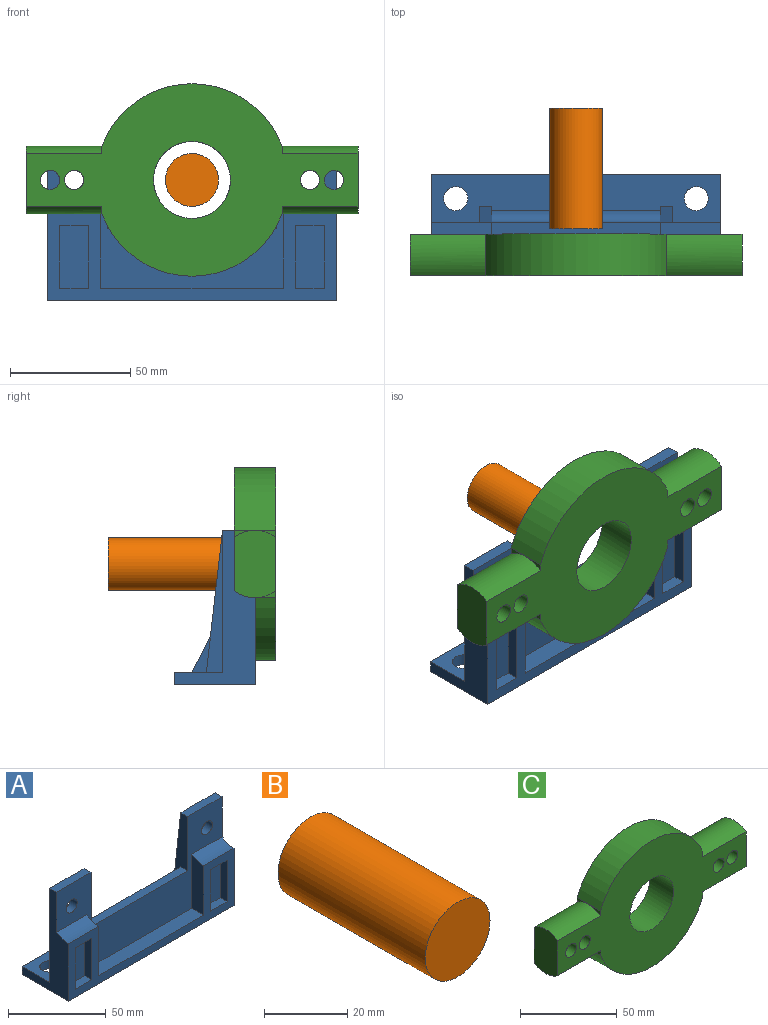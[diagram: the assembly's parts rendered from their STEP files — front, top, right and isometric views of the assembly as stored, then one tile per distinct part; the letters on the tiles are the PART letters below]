
ASSEMBLY  parts=3 mates=2
PART A: 63 faces, bbox 120x33.6x64 mm
  f0: plane 59x20mm, normal (0,1,0), area 1129.7mm2, adj f1,f11,f13,f19,f31
  f1: plane 120x20mm, normal (0,0,1), area 1786.8mm2, adj f0,f5,f9,f10,f11,f16,f17,f22
  f2: plane 32.5x20mm, normal (0,1,0), area 425mm2, adj f3,f9,f25,f33,f58,f59,f60,f61
  f3: plane 70x5mm, normal (0,0,1), area 350mm2, adj f2,f4,f7,f9,f24,f27
  f4: plane 32.5x20mm, normal (0,1,0), area 425mm2, adj f3,f26,f27,f32,f53,f54,f55,f56
  f5: plane 59x20mm, normal (0,1,0), area 1129.7mm2, adj f1,f8,f18,f22,f29
  f6: plane 76x8.6mm, normal (0,0,1), area 653.6mm2, adj f7,f12,f14,f23
  f7: plane 120x59mm, normal (0,-1,0), area 3105.5mm2, adj f3,f6,f8,f9,f11,f12,f13,f18
  f8: plane 25x5mm, normal (0,0,1), area 125mm2, adj f5,f7,f9,f22,f28
  f9: plane 59x11.73mm, normal (-1,0,0), area 363.3mm2, adj f1,f2,f3,f7,f8,f28,f33
  f10: plane 120x5mm, normal (0,1,0), area 600mm2, adj f1,f11,f15,f22
  f11: plane 64x33.6mm, normal (-1,0,0), area 737.7mm2, adj f0,f1,f7,f10,f13,f14,f15,f20
  f12: plane 33.95x8.6mm, normal (1,0,0), area 274.7mm2, adj f6,f7,f14,f20
  f13: plane 25x5mm, normal (0,0,1), area 125mm2, adj f0,f7,f11,f27,f30
  f14: plane 120x36mm, normal (0,-1,0), area 1340mm2, adj f6,f11,f12,f15,f20,f21,f22,f23
  f15: plane 120x33.6mm, normal (0,0,-1), area 1790.9mm2, adj f10,f11,f14,f16,f17,f22,f34,f35
  f16: cylinder r=5mm len=10mm, axis (0,0,1), area 157.1mm2, adj f1,f15
  f17: cylinder r=5mm len=10mm, axis (0,0,1), area 157.1mm2, adj f1,f15
  f18: cylinder r=4mm len=8mm, axis (0,1,0), area 125.7mm2, adj f5,f7
  f19: cylinder r=4mm len=8mm, axis (0,1,0), area 125.7mm2, adj f0,f7
  f20: cylinder r=14mm len=22mm, axis (1,0,0), area 203.7mm2, adj f7,f11,f12,f14
  f21: cylinder r=14mm len=22mm, axis (-1,0,0), area 203.7mm2, adj f7,f14,f22,f23
  f22: plane 64x33.6mm, normal (1,0,0), area 737.7mm2, adj f1,f5,f7,f8,f10,f14,f15,f21
  f23: plane 33.95x8.6mm, normal (-1,0,0), area 274.7mm2, adj f6,f7,f14,f21
  f24: plane 25x12.75mm, normal (0,0.89,0.45), area 140.3mm2, adj f1,f3,f25,f26
  f25: plane 25x12.75mm, normal (1,0,0), area 154mm2, adj f1,f2,f24,f33
  f26: plane 25x12.75mm, normal (-1,0,0), area 154mm2, adj f1,f4,f24,f32
  f27: plane 59x11.73mm, normal (1,0,0), area 363.3mm2, adj f1,f3,f4,f7,f13,f30,f32
  f28: plane 59x6.73mm, normal (0,0.99,0.11), area 296.9mm2, adj f1,f8,f9,f29
  f29: plane 59x6.73mm, normal (1,0,0), area 198.7mm2, adj f1,f5,f28
  f30: plane 59x6.73mm, normal (0,0.99,0.11), area 296.9mm2, adj f1,f13,f27,f31
  f31: plane 59x6.73mm, normal (-1,0,0), area 198.7mm2, adj f0,f1,f30
  f32: cylinder r=5mm len=32.5mm, axis (1,0,0), area 255.3mm2, adj f1,f4,f26,f27
  f33: cylinder r=5mm len=32.5mm, axis (1,0,0), area 255.3mm2, adj f1,f2,f9,f25
  f34: plane 16x2mm, normal (0,-1,0), area 32mm2, adj f15,f35,f41,f42
  f35: plane 16x2mm, normal (1,0,0), area 32mm2, adj f15,f34,f36,f42
  f36: plane 78x2mm, normal (0,-1,0), area 156mm2, adj f15,f35,f37,f42
  f37: plane 16x2mm, normal (-1,0,0), area 32mm2, adj f15,f36,f38,f42
  f38: plane 16x2mm, normal (0,-1,0), area 32mm2, adj f15,f37,f39,f42
  f39: plane 7.6x2mm, normal (-1,0,0), area 15.2mm2, adj f15,f38,f40,f42
  f40: plane 110x2mm, normal (0,1,0), area 220mm2, adj f15,f39,f41,f42
  f41: plane 7.6x2mm, normal (1,0,0), area 15.2mm2, adj f15,f34,f40,f42
  f42: plane 110x23.6mm, normal (0,0,-1), area 2084mm2, adj f34,f35,f36,f37,f38,f39,f40,f41
  f43: plane 26x5mm, normal (1,0,0), area 130mm2, adj f14,f44,f46,f47
  f44: plane 12x5mm, normal (0,0,1), area 60mm2, adj f14,f43,f45,f47
  f45: plane 26x5mm, normal (-1,0,0), area 130mm2, adj f14,f44,f46,f47
  f46: plane 12x5mm, normal (0,0,-1), area 60mm2, adj f14,f43,f45,f47
  f47: plane 26x12mm, normal (0,-1,0), area 312mm2, adj f43,f44,f45,f46
  f48: plane 26x5mm, normal (1,0,0), area 130mm2, adj f14,f49,f51,f52
  f49: plane 12x5mm, normal (0,0,1), area 60mm2, adj f14,f48,f50,f52
  f50: plane 26x5mm, normal (-1,0,0), area 130mm2, adj f14,f49,f51,f52
  f51: plane 12x5mm, normal (0,0,-1), area 60mm2, adj f14,f48,f50,f52
  f52: plane 26x12mm, normal (0,-1,0), area 312mm2, adj f48,f49,f50,f51
  f53: plane 10x2mm, normal (-1,0,0), area 20mm2, adj f4,f54,f56,f57
  f54: plane 22.5x2mm, normal (0,0,1), area 45mm2, adj f4,f53,f55,f57
  f55: plane 10x2mm, normal (1,0,0), area 20mm2, adj f4,f54,f56,f57
  f56: plane 22.5x2mm, normal (0,0,-1), area 45mm2, adj f4,f53,f55,f57
  f57: plane 22.5x10mm, normal (0,1,0), area 225mm2, adj f53,f54,f55,f56
  f58: plane 10x2mm, normal (-1,0,0), area 20mm2, adj f2,f59,f61,f62
  f59: plane 22.5x2mm, normal (0,0,1), area 45mm2, adj f2,f58,f60,f62
  f60: plane 10x2mm, normal (1,0,0), area 20mm2, adj f2,f59,f61,f62
  f61: plane 22.5x2mm, normal (0,0,-1), area 45mm2, adj f2,f58,f60,f62
  f62: plane 22.5x10mm, normal (0,1,0), area 225mm2, adj f58,f59,f60,f61
PART B: 3 faces, bbox 22x50x22 mm
  f0: cylinder r=11mm len=50mm, axis (0,1,0), area 3455.8mm2, adj f1,f2
  f1: plane 22x22mm, normal (0,-1,0), area 380.1mm2, adj f0
  f2: plane 22x22mm, normal (0,1,0), area 380.1mm2, adj f0
PART C: 27 faces, bbox 138x17.2x80 mm
  f0: plane 138x80mm, normal (0,-1,0), area 5319.8mm2, adj f1,f2,f4,f5,f6,f7,f8,f9
  f1: plane 17.2x0.03mm, normal (0,0,1), area 0.5mm2, adj f0,f3,f12,f24,f26
  f2: plane 17.2x0.03mm, normal (0,0,-1), area 0.5mm2, adj f0,f3,f13,f22,f25
  f3: plane 138x80mm, normal (0,1,0), area 5319.8mm2, adj f1,f2,f4,f5,f6,f7,f8,f9
  f4: plane 28x17.2mm, normal (-1,0,0), area 449.3mm2, adj f0,f3,f15,f17
  f5: plane 17.2x0.03mm, normal (0,0,1), area 0.5mm2, adj f0,f3,f12,f18,f20
  f6: plane 17.2x0.03mm, normal (0,0,-1), area 0.5mm2, adj f0,f3,f13,f16,f19
  f7: plane 28x17.2mm, normal (1,0,0), area 449.3mm2, adj f0,f3,f21,f23
  f8: cylinder r=4mm len=17.2mm, axis (0,-1,0), area 432.3mm2, adj f0,f3
  f9: cylinder r=4mm len=17.2mm, axis (0,-1,0), area 432.3mm2, adj f0,f3
  f10: cylinder r=4mm len=17.2mm, axis (0,-1,0), area 432.3mm2, adj f0,f3
  f11: cylinder r=4mm len=17.2mm, axis (0,-1,0), area 432.3mm2, adj f0,f3
  f12: cylinder r=40mm len=74.94mm, axis (0,-1,0), area 1669.4mm2, adj f0,f1,f3,f5
  f13: cylinder r=40mm len=74.94mm, axis (0,-1,0), area 1669.4mm2, adj f0,f2,f3,f6
  f14: cylinder r=16mm len=32mm, axis (0,-1,0), area 1729.1mm2, adj f0,f3
  f15: cylinder r=14mm len=31.5mm, axis (-1,0,0), area 583.4mm2, adj f0,f3,f4,f16,f19
  f16: plane 8.6x2.95mm, normal (-1,0,0), area 8.1mm2, adj f0,f6,f15
  f17: cylinder r=14mm len=31.5mm, axis (-1,0,0), area 583.4mm2, adj f0,f3,f4,f18,f20
  f18: plane 8.6x2.95mm, normal (-1,0,0), area 8.1mm2, adj f0,f5,f17
  f19: plane 8.6x2.95mm, normal (-1,0,0), area 8.1mm2, adj f3,f6,f15
  f20: plane 8.6x2.95mm, normal (-1,0,0), area 8.1mm2, adj f3,f5,f17
  f21: cylinder r=14mm len=31.5mm, axis (1,0,0), area 583.4mm2, adj f0,f3,f7,f22,f25
  f22: plane 8.6x2.95mm, normal (1,0,0), area 8.1mm2, adj f2,f3,f21
  f23: cylinder r=14mm len=31.5mm, axis (1,0,0), area 583.4mm2, adj f0,f3,f7,f24,f26
  f24: plane 8.6x2.95mm, normal (1,0,0), area 8.1mm2, adj f1,f3,f23
  f25: plane 8.6x2.95mm, normal (1,0,0), area 8.1mm2, adj f0,f2,f21
  f26: plane 8.6x2.95mm, normal (1,0,0), area 8.1mm2, adj f0,f1,f23
PLACE A t=(-8.85,-5.24,0.71)mm
PLACE B t=(-8.85,39.39,0.71)mm
PLACE C t=(-8.85,-5.07,0.71)mm
MATE slider A.f18 <-> C.f8  axis (0,1,0) through (40.15,-25.24,10.71)mm
MATE slider C.f12 <-> B.f0  axis (0,1,0) through (-8.85,-30.07,10.71)mm
